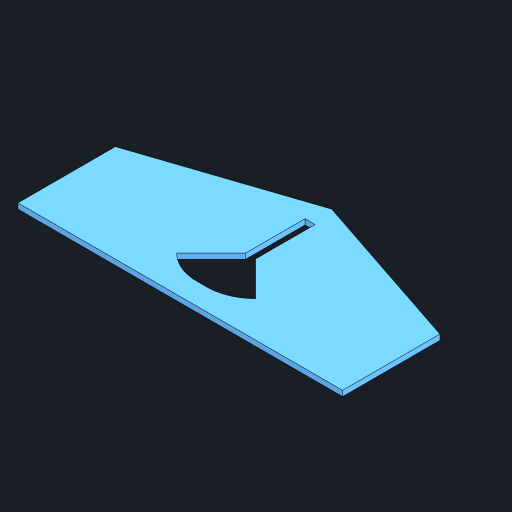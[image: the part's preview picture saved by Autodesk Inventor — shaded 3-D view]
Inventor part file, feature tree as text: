
AUTODESK INVENTOR PART (.ipt)
format: ipt  version: 2023 (Build 270158000, 158)  size: 132,608 bytes
history: native  units: mm
features: other x1, extrude x1, sketch x1
ambient origin geometry x8: Origin, YZ Plane, XZ Plane, XY Plane, X Axis, Y Axis, Z Axis, Center Point
bodies: Body1 (feature_tree)
feature tree (3):
  other  "ソリッド1"
  extrude  "押し出し1"  Depth=9.3mm
  sketch  "スケッチ1"
